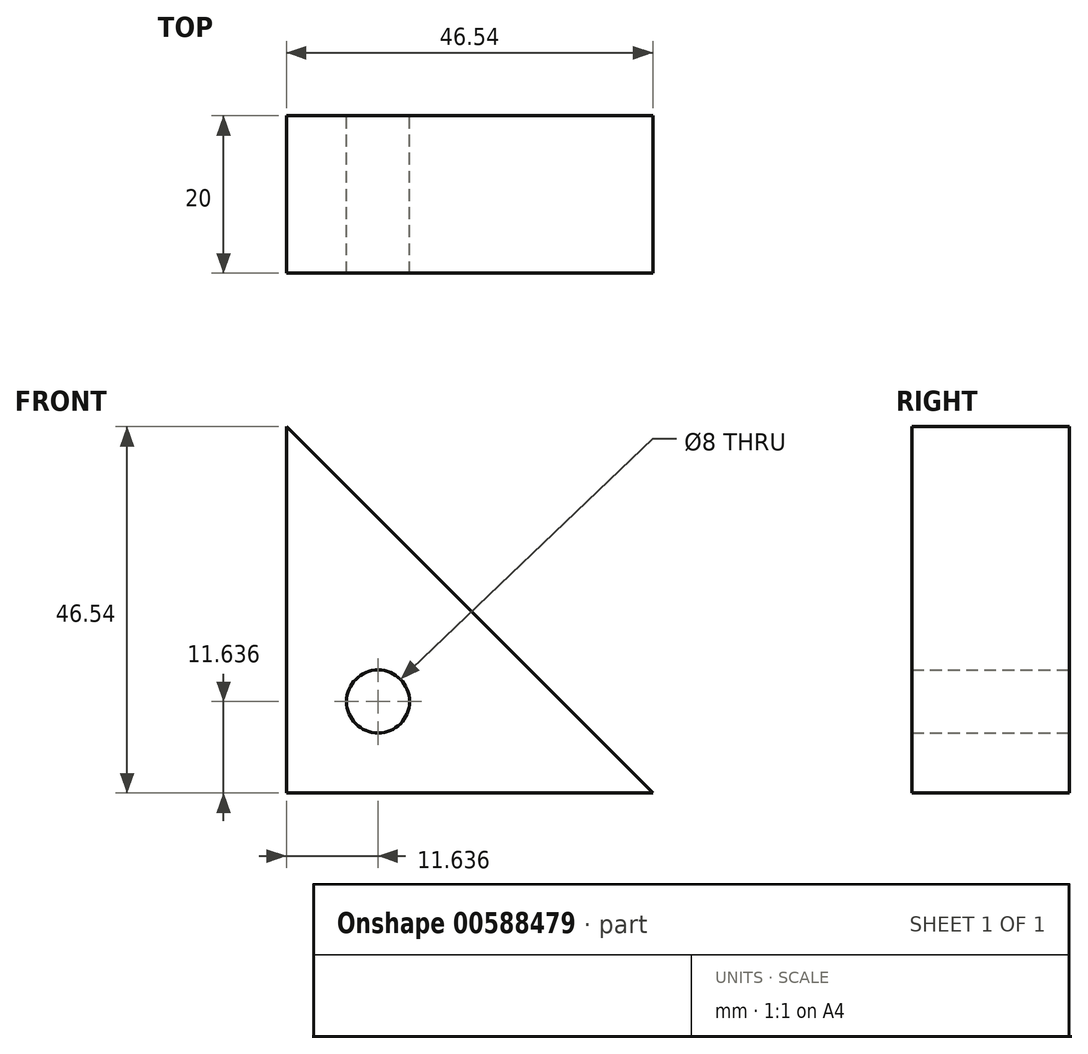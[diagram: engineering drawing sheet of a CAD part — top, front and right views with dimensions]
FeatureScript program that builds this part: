
annotation { "Feature Type Name" : "Feature", "Feature Type Description" : "" }
export const myFeature = defineFeature(function(context is Context, id is Id, definition is map)
    precondition{}
    {
        {
            var Q0;
            Q0=qCreatedBy(makeId("Front.planeOp"),FACE);
            var sketch = newSketch(context, id + "F0", { "sketchPlane" : qUnion([Q0])});
            skLineSegment(sketch, "E0", {"start": v(0, 0) * mm, "end": v(0, 46.54) * mm});
            skLineSegment(sketch, "E1", {"start": v(0, 46.54) * mm, "end": v(46.54, 0) * mm});
            skLineSegment(sketch, "E2", {"start": v(46.54, 0) * mm, "end": v(0, 0) * mm});
            skCircle(sketch, "E3", {"center": v(11.64, 11.64) * mm, "radius": 4 * mm});
            skLineSegment(sketch, "E4", {"start": v(0, 0) * mm, "end": v(11.64, 11.64) * mm, "construction": true});
            skLineSegment(sketch, "E5", {"start": v(11.64, 11.64) * mm, "end": v(23.27, 23.27) * mm, "construction": true});
            skSolve(sketch);
        }
        {
            var Q0;
            Q0=makeQuery(id+"F0.imprint","IMPRINT",FACE,{"disambiguationData":[TD([[makeQuery(id+"F0.imprint","IMPRINT",EDGE,{"derivedFrom":sQuery(id+"F0.wireOp",EDGE,"E0")}),-1.0]])]});
            extrude(context, id + "F1", {"entities" : qUnion([Q0]), "depth" : 20 * mm, "offsetDistance" : 25 * mm});
        }
    });
